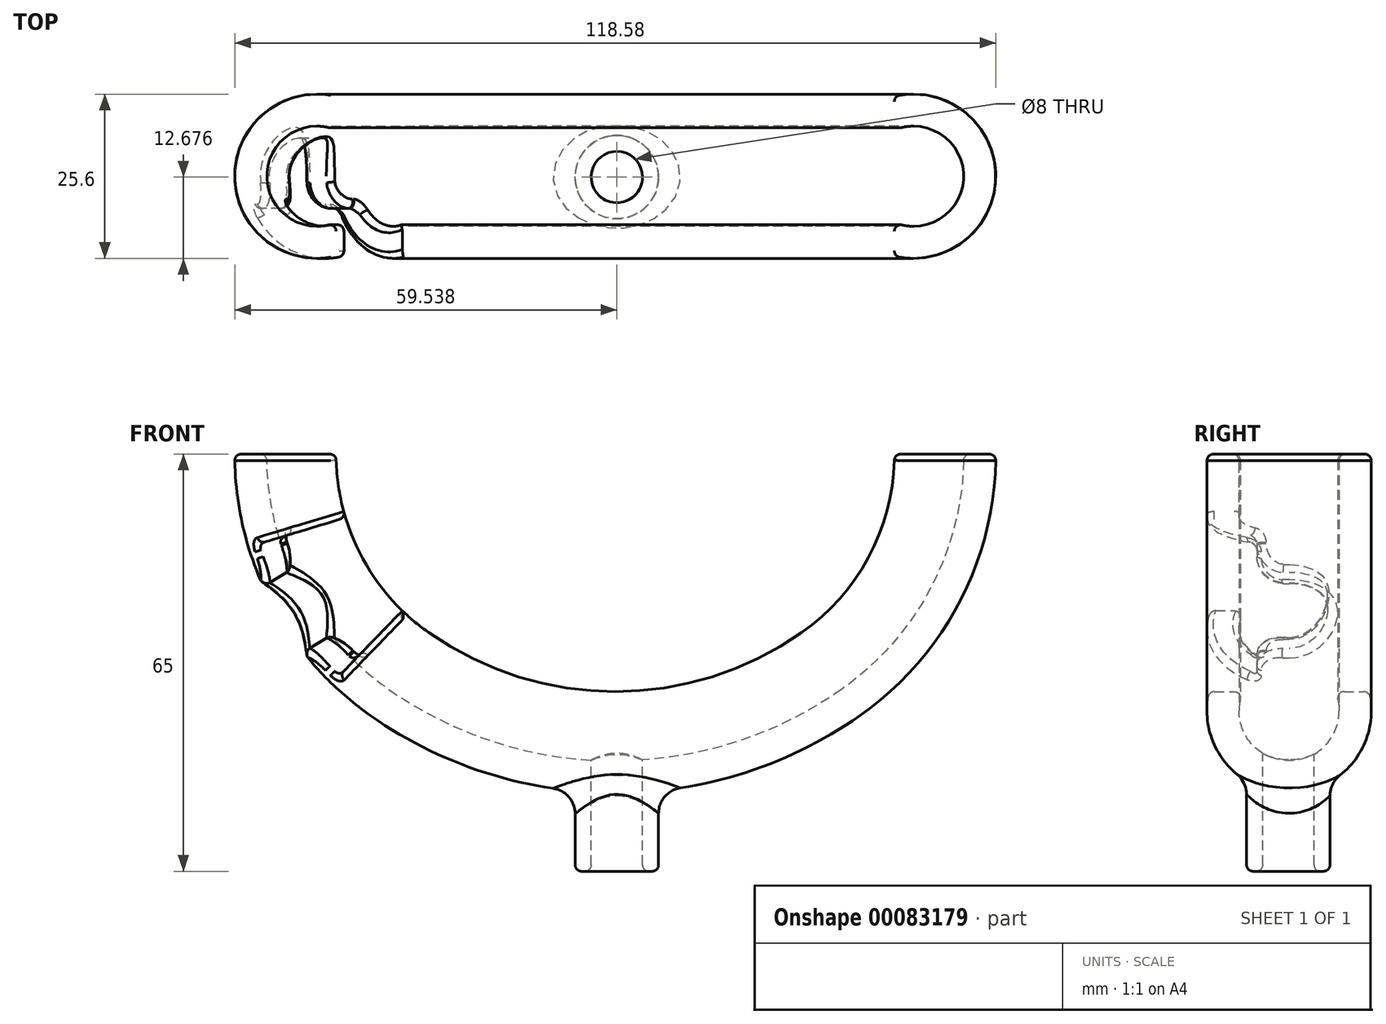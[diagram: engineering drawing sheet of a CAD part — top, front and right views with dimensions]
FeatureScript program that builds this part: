
annotation { "Feature Type Name" : "Feature", "Feature Type Description" : "" }
export const myFeature = defineFeature(function(context is Context, id is Id, definition is map)
    precondition{}
    {
        {
            var Q0;
            Q0=qCreatedBy(makeId("Front.planeOp"),FACE);
            var sketch = newSketch(context, id + "F0", { "sketchPlane" : qUnion([Q0])});
            skLineSegment(sketch, "E0", {"start": v(-46.5, 60.82) * mm, "end": v(-46.5, 0) * mm, "construction": true});
            skLineSegment(sketch, "E1", {"start": v(46.5, 60.82) * mm, "end": v(46.5, 0) * mm, "construction": true});
            skLineSegment(sketch, "E2", {"start": v(-46.5, 60.82) * mm, "end": v(46.5, 60.82) * mm, "construction": true});
            skArc(sketch, "E3", {"start": v(-30.75, -30.29) * mm, "mid": v(0, -40) * mm, "end": v(30.75, -30.29) * mm});
            skArc(sketch, "E4", {"start": v(-46.5, 0) * mm, "mid": v(-42.33, -17.07) * mm, "end": v(-30.75, -30.29) * mm});
            skArc(sketch, "E5", {"start": v(30.75, -30.29) * mm, "mid": v(42.33, -17.07) * mm, "end": v(46.5, 0) * mm});
            skSolve(sketch);
        }
        {
            var Q0;
            Q0=qCreatedBy(makeId("Top.planeOp"),FACE);
            var sketch = newSketch(context, id + "F11", { "sketchPlane" : qUnion([Q0])});
            skLineSegment(sketch, "E6", {"start": v(0, 87.49) * mm, "end": v(0, 87.49) * mm});
            skArc(sketch, "E7", {"start": v(43.5, -7.2) * mm, "mid": v(54.3, 0) * mm, "end": v(43.5, 7.2) * mm});
            skLineSegment(sketch, "E8", {"start": v(43.5, 12.44) * mm, "end": v(43.5, -12.44) * mm, "construction": true});
            skArc(sketch, "E9.0", {"start": v(43.5, -12.44) * mm, "mid": v(59.3, 0) * mm, "end": v(43.5, 12.44) * mm});
            skLineSegment(sketch, "E10", {"start": v(43.5, 12.44) * mm, "end": v(43.5, 7.2) * mm});
            skLineSegment(sketch, "E11", {"start": v(43.5, -7.2) * mm, "end": v(43.5, -12.44) * mm});
            skCircle(sketch, "E12", {"center": v(0.25, -0.12) * mm, "radius": 4 * mm});
            skCircle(sketch, "E13", {"center": v(0.25, -0.12) * mm, "radius": 6.5 * mm});
            skSolve(sketch);
        }
        {
            var Q0;
            Q0=makeQuery(id+"F11.imprint","IMPRINT",FACE,{"disambiguationData":[TD([[makeQuery(id+"F11.imprint","IMPRINT",EDGE,{"derivedFrom":sQuery(id+"F11.wireOp",EDGE,"E7")}),-1.0]])]});
            var Q1;
            Q1 = qConstructionFilter(qBodyType(qCreatedBy(id + "F0" ,EDGE), BodyType.WIRE), ConstructionObject.NO);
            sweep(context, id + "F1", {"profiles" : qUnion([Q0]), "path" : qUnion([Q1])});
        }
        {
            var Q0;
            Q0=makeQuery(id+"F11.imprint","IMPRINT",FACE,{"disambiguationData":[TD([[makeQuery(id+"F11.imprint","IMPRINT",EDGE,{"derivedFrom":sQuery(id+"F11.wireOp",EDGE,"E12")}),1.0]])]});
            extrude(context, id + "F2", {"entities" : qUnion([Q0]), "operationType" : NewBodyOperationType.REMOVE, "endBound" : BoundingType.THROUGH_ALL, "oppositeDirection" : true, "depth" : 25 * mm});
        }
        {
            var Q0;
            Q0=makeQuery(id+"F11.imprint","IMPRINT",FACE,{"disambiguationData":[TD([[makeQuery(id+"F11.imprint","IMPRINT",EDGE,{"derivedFrom":sQuery(id+"F11.wireOp",EDGE,"E12")}),-1.0]])]});
            var Q1;
            Q1=makeQuery(id+"F1.opSweep","SWEPT_BODY",BODY,{"disambiguationData":[OSD([sQuery(id+"F0.wireOp",EDGE,"E4"),sQuery(id+"F11.wireOp",EDGE,"E7"),sQuery(id+"F11.wireOp",EDGE,"E9.0"),sQuery(id+"F11.wireOp",EDGE,"E10"),sQuery(id+"F11.wireOp",EDGE,"E11")])]});
            extrude(context, id + "F3", {"entities" : qUnion([Q0]), "oppositeDirection" : true, "depth" : 65 * mm, "hasSecondDirection" : true, "secondDirectionBound" : SecondDirectionBoundingType.UP_TO_BODY, "secondDirectionOppositeDirection" : true, "secondDirectionBoundEntityBody" : qUnion([Q1]), "secondDirectionDepth" : 70 * mm});
        }
        {
            var Q0;
            Q0=qCreatedBy(makeId("Front.planeOp"),FACE);
            var sketch = newSketch(context, id + "F4", { "sketchPlane" : qUnion([Q0])});
            skArc(sketch, "E14.0", {"start": v(-29.03, -27.83) * mm, "mid": v(-39.67, -15.69) * mm, "end": v(-43.5, 0) * mm, "construction": true});
            skLineSegment(sketch, "E15", {"start": v(-42.03, -9.9) * mm, "end": v(-62.86, -16.22) * mm});
            skLineSegment(sketch, "E16", {"start": v(-62.86, -16.22) * mm, "end": v(-48.33, -40.03) * mm});
            skLineSegment(sketch, "E17", {"start": v(-48.33, -40.03) * mm, "end": v(-33.17, -24.4) * mm});
            skArc(sketch, "E18", {"start": v(-42.03, -9.9) * mm, "mid": v(-38.52, -17.7) * mm, "end": v(-33.17, -24.4) * mm});
            skLineSegment(sketch, "E19", {"start": v(-55.6, -28.13) * mm, "end": v(-38.52, -17.7) * mm});
            skLineSegment(sketch, "E20", {"start": v(-52.47, -33.25) * mm, "end": v(-34.94, -22.55) * mm});
            skLineSegment(sketch, "E21.MirrorCS", {"start": v(-58.72, -23) * mm, "end": v(-41.2, -12.3) * mm});
            skSolve(sketch);
        }
        {
            var Q0;
            Q0=makeQuery(id+"F4.imprint","IMPRINT",FACE,{"disambiguationData":[TD([[makeQuery(id+"F4.imprint","IMPRINT",EDGE,{"derivedFrom":sQuery(id+"F4.wireOp",EDGE,"E15")}),1.0]])]});
            var Q1;
            {var subQ0=sQuery(id+"F4.wireOp",EDGE,"E17");Q1=makeQuery(id+"F4.imprint","IMPRINT",FACE,{"disambiguationData":[TD([[makeQuery(id+"F4.imprint","IMPRINT",EDGE,{"derivedFrom":subQ0}),1.0]])]});}
            var Q2;
            {var subQ0=sQuery(id+"F4.wireOp",EDGE,"E19");Q2=makeQuery(id+"F4.imprint","IMPRINT",FACE,{"disambiguationData":[TD([[makeQuery(id+"F4.imprint","IMPRINT",EDGE,{"derivedFrom":subQ0}),-1.0]])]});}
            var Q3;
            {var subQ0=sQuery(id+"F4.wireOp",EDGE,"E19");Q3=makeQuery(id+"F4.imprint","IMPRINT",FACE,{"disambiguationData":[TD([[makeQuery(id+"F4.imprint","IMPRINT",EDGE,{"derivedFrom":subQ0}),1.0]])]});}
            extrude(context, id + "F5", {"entities" : qUnion([Q0, Q1, Q2, Q3]), "operationType" : NewBodyOperationType.REMOVE, "depth" : 25 * mm, "hasSecondDirection" : true, "secondDirectionOppositeDirection" : false, "secondDirectionDepth" : 5 * mm});
        }
        {
            var Q0;
            {var subQ0=sQuery(id+"F4.wireOp",EDGE,"E19");Q0=makeQuery(id+"F4.imprint","IMPRINT",FACE,{"disambiguationData":[TD([[makeQuery(id+"F4.imprint","IMPRINT",EDGE,{"derivedFrom":subQ0}),-1.0]])]});}
            var Q1;
            Q1=sQuery(id+"F4.wireOp",EDGE,"E19");
            revolve(context, id + "F6", {"operationType" : NewBodyOperationType.REMOVE, "entities" : qUnion([Q0]), "axis" : qUnion([Q1]), "revolveType" : RevolveType.FULL, "oppositeDirection" : true});
        }
        {
            var Q0;
            {var subQ0=sQuery(id+"F4.wireOp",EDGE,"E19");Q0=makeQuery(id+"F4.imprint","IMPRINT",FACE,{"disambiguationData":[TD([[makeQuery(id+"F4.imprint","IMPRINT",EDGE,{"derivedFrom":subQ0}),1.0]])]});}
            var Q1;
            {var subQ0=sQuery(id+"F4.wireOp",EDGE,"E19");Q1=makeQuery(id+"F4.imprint","IMPRINT",FACE,{"disambiguationData":[TD([[makeQuery(id+"F4.imprint","IMPRINT",EDGE,{"derivedFrom":subQ0}),-1.0]])]});}
            extrude(context, id + "F7", {"entities" : qUnion([Q0, Q1]), "operationType" : NewBodyOperationType.REMOVE, "depth" : 25 * mm});
        }
        {
            var Q0;
            Q0=makeQuery(id+"F1.opSweep","SWEPT_FACE",FACE,{"disambiguationData":[OSD([sQuery(id+"F0.wireOp",EDGE,"E4"),sQuery(id+"F11.wireOp",EDGE,"E9.0")])]});
            var Q1;
            Q1=makeQuery(id+"F1.opSweep","SWEPT_FACE",FACE,{"disambiguationData":[OSD([sQuery(id+"F0.wireOp",EDGE,"E4"),sQuery(id+"F11.wireOp",EDGE,"E7")])]});
            var Q2;
            Q2=makeQuery(id+"F1.opSweep","SWEPT_FACE",FACE,{"disambiguationData":[OSD([sQuery(id+"F0.wireOp",EDGE,"E5"),sQuery(id+"F11.wireOp",EDGE,"E7")])]});
            var Q3;
            Q3=makeQuery(id+"F1.opSweep","SWEPT_FACE",FACE,{"disambiguationData":[OSD([sQuery(id+"F0.wireOp",EDGE,"E3"),sQuery(id+"F11.wireOp",EDGE,"E7")])]});
            var Q4;
            Q4=makeQuery(id+"F1.opSweep","SWEPT_FACE",FACE,{"disambiguationData":[OSD([sQuery(id+"F0.wireOp",EDGE,"E5"),sQuery(id+"F11.wireOp",EDGE,"E9.0")])]});
            var Q5;
            {var subQ0=sQuery(id+"F11.wireOp",EDGE,"E12");var subQ1=sQuery(id+"F11.wireOp",EDGE,"E13");Q5=makeQuery(id+"F3.opExtrude","CAP_FACE",FACE,{"disambiguationData":[OSD([subQ0,subQ1]),topologyDisambiguationEdgeConnected([makeQuery(id+"F11.imprint","IMPRINT",EDGE,{"derivedFrom":subQ0})])],"isStart":false});}
            var Q6;
            Q6=makeQuery(id+"F1.opSweep","CAP_FACE",FACE,{"disambiguationData":[OSD([sQuery(id+"F0.wireOp",VERTEX,"E5.end"),sQuery(id+"F11.wireOp",EDGE,"E7"),sQuery(id+"F11.wireOp",EDGE,"E9.0"),sQuery(id+"F11.wireOp",EDGE,"E10"),sQuery(id+"F11.wireOp",EDGE,"E11")])],"isStart":true});
            var Q7;
            Q7=makeQuery(id+"F1.opSweep","CAP_EDGE",EDGE,{"disambiguationData":[OSD([sQuery(id+"F0.wireOp",VERTEX,"E4.start"),sQuery(id+"F11.wireOp",EDGE,"E10")])],"isStart":false});
            var Q8;
            Q8=makeQuery(id+"F1.opSweep","CAP_EDGE",EDGE,{"disambiguationData":[OSD([sQuery(id+"F0.wireOp",VERTEX,"E4.start"),sQuery(id+"F11.wireOp",EDGE,"E11")])],"isStart":false});
            var Q9;
            Q9=makeQuery(id+"F5.boolean.opBoolean","COPY",EDGE,{"derivedFrom":makeQuery(id+"F5.opExtrude","SWEPT_EDGE",EDGE,{"disambiguationData":[OSD([sQuery(id+"F4.wireOp",EDGE,"E17"),sQuery(id+"F4.wireOp",EDGE,"E18")])]})});
            var Q10;
            Q10=makeQuery(id+"F5.boolean.opBoolean","COPY",EDGE,{"derivedFrom":makeQuery(id+"F5.opExtrude","SWEPT_EDGE",EDGE,{"disambiguationData":[OSD([sQuery(id+"F4.wireOp",EDGE,"E15"),sQuery(id+"F4.wireOp",EDGE,"E18")])]})});
            var Q11;
            Q11=makeQuery(id+"F5.boolean.opBoolean","COPY",EDGE,{"derivedFrom":makeQuery(id+"F5.opExtrude","CAP_EDGE",EDGE,{"disambiguationData":[OSD([sQuery(id+"F4.wireOp",EDGE,"E17")])],"isStart":true})});
            var Q12;
            Q12=makeQuery(id+"F5.boolean.opBoolean","COPY",EDGE,{"derivedFrom":makeQuery(id+"F5.opExtrude","CAP_EDGE",EDGE,{"disambiguationData":[OSD([sQuery(id+"F4.wireOp",EDGE,"E15")])],"isStart":true})});
            var Q13;
            Q13=makeQuery(id+"F2.boolean.opBoolean","INTERSECT",EDGE,{"derivedFrom":[makeQuery(id+"F1.opSweep","SWEPT_FACE",FACE,{"disambiguationData":[OSD([sQuery(id+"F0.wireOp",EDGE,"E3"),sQuery(id+"F11.wireOp",EDGE,"E7")])]}),makeQuery(id+"F2.opExtrude","SWEPT_FACE",FACE,{"disambiguationData":[OSD([sQuery(id+"F11.wireOp",EDGE,"E12")])]})]});
            var Q14;
            Q14=makeQuery(id+"F1.opSweep","SWEPT_EDGE",EDGE,{"disambiguationData":[OSD([sQuery(id+"F0.wireOp",EDGE,"E3"),sQuery(id+"F11.wireOp",EDGE,"E9.0"),sQuery(id+"F11.wireOp",EDGE,"E11")])]});
            var Q15;
            Q15=makeQuery(id+"F1.opSweep","SWEPT_EDGE",EDGE,{"disambiguationData":[OSD([sQuery(id+"F0.wireOp",EDGE,"E3"),sQuery(id+"F11.wireOp",EDGE,"E9.0"),sQuery(id+"F11.wireOp",EDGE,"E10")])]});
            fillet(context, id + "F8", {"entities" : qUnion([Q0, Q1, Q2, Q3, Q4, Q5, Q6, Q7, Q8, Q9, Q10, Q11, Q12, Q13, Q14, Q15]), "radius" : 1 * mm, "tangentPropagation" : true, "allowEdgeOverflow" : false});
        }
        {
            var Q0;
            Q0=makeQuery(id+"F1.opSweep","SWEPT_BODY",BODY,{"disambiguationData":[OSD([sQuery(id+"F0.wireOp",EDGE,"E4"),sQuery(id+"F11.wireOp",EDGE,"E7"),sQuery(id+"F11.wireOp",EDGE,"E9.0"),sQuery(id+"F11.wireOp",EDGE,"E10"),sQuery(id+"F11.wireOp",EDGE,"E11")])]});
            var Q1;
            Q1=makeQuery(id+"F3.opExtrude","SWEPT_BODY",BODY,{"disambiguationData":[OSD([sQuery(id+"F11.wireOp",EDGE,"E12"),sQuery(id+"F11.wireOp",EDGE,"E13")])]});
            booleanBodies(context, id + "F9", {"operationType" : BooleanOperationType.UNION, "tools" : qUnion([Q0, Q1])});
        }
        {
            var Q0;
            Q0=makeQuery(id+"F9.opBoolean","INTERSECT",EDGE,{"derivedFrom":[makeQuery(id+"F1.opSweep","SWEPT_FACE",FACE,{"disambiguationData":[OSD([sQuery(id+"F0.wireOp",EDGE,"E3"),sQuery(id+"F11.wireOp",EDGE,"E9.0")])]}),makeQuery(id+"F3.opExtrude","SWEPT_FACE",FACE,{"disambiguationData":[OSD([sQuery(id+"F11.wireOp",EDGE,"E13")])]})]});
            var Q1;
            {var subQ1=sQuery(id+"F4.wireOp",EDGE,"E15");Q1=makeQuery(id+"F7.boolean.opBoolean","INTERSECT",EDGE,{"derivedFrom":[makeQuery(id+"F6.boolean.opBoolean","SPLIT",FACE,{"disambiguationData":[TD([makeQuery(id+"F5.boolean.opBoolean","COPY",FACE,{"derivedFrom":makeQuery(id+"F5.opExtrude","SWEPT_FACE",FACE,{"disambiguationData":[OSD([subQ1])]})})])],"derivedFrom":makeQuery(id+"F5.boolean.opBoolean","COPY",FACE,{"derivedFrom":makeQuery(id+"F5.opExtrude","CAP_FACE",FACE,{"disambiguationData":[OSD([subQ1,sQuery(id+"F4.wireOp",EDGE,"E16"),sQuery(id+"F4.wireOp",EDGE,"E17"),sQuery(id+"F4.wireOp",EDGE,"E18")])],"isStart":true})})}),makeQuery(id+"F7.opExtrude","SWEPT_FACE",FACE,{"disambiguationData":[OSD([sQuery(id+"F4.wireOp",EDGE,"E21.MirrorCS")])]})]});}
            var Q2;
            {var subQ0=sQuery(id+"F4.wireOp",EDGE,"E20");var subQ2=sQuery(id+"F4.wireOp",EDGE,"E17");Q2=makeQuery(id+"F7.boolean.opBoolean","INTERSECT",EDGE,{"derivedFrom":[makeQuery(id+"F6.boolean.opBoolean","SPLIT",FACE,{"disambiguationData":[TD([makeQuery(id+"F5.boolean.opBoolean","COPY",FACE,{"derivedFrom":makeQuery(id+"F5.opExtrude","SWEPT_FACE",FACE,{"disambiguationData":[OSD([subQ2])]})})])],"derivedFrom":makeQuery(id+"F5.boolean.opBoolean","COPY",FACE,{"derivedFrom":makeQuery(id+"F5.opExtrude","CAP_FACE",FACE,{"disambiguationData":[OSD([sQuery(id+"F4.wireOp",EDGE,"E15"),sQuery(id+"F4.wireOp",EDGE,"E16"),subQ2,sQuery(id+"F4.wireOp",EDGE,"E18")])],"isStart":true})})}),makeQuery(id+"F7.opExtrude","SWEPT_FACE",FACE,{"disambiguationData":[OSD([subQ0])]})]});}
            fillet(context, id + "F10", {"entities" : qUnion([Q0, Q1, Q2]), "radius" : 4 * mm, "tangentPropagation" : true, "allowEdgeOverflow" : false});
        }
    });
